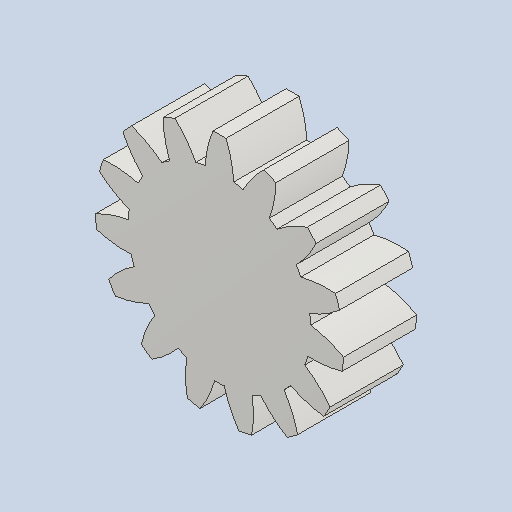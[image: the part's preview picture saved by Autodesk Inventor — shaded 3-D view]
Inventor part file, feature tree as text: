
AUTODESK INVENTOR PART (.ipt)
format: ipt  version: 2023 (Build 270158000, 158)  size: 195,072 bytes
history: native  units: mm (DEFAULTED — no unit token found)
features: plane x3, other x3, sketch x2, extrude x1
ambient origin geometry x8: Origin, YZ Plane, XZ Plane, XY Plane, X Axis, Y Axis, Z Axis, Center Point
bodies: Solid1 (feature_tree)
feature tree (9):
  extrude  "Extrusion1"  Depth=10.0mm TaperAngle=0.0deg
  plane  "Work Plane2"
  plane  "Work Plane8"
  plane  "Work Plane9"
  other  "Spur Gear"
  sketch  "Sketch1"  dims[d0=34.0mm d1=10.0mm d2=0.0mm]
  sketch  "Sketch2"  dims[d3=30.0mm d4=10.0mm d5=0.0mm d16=45.0mm d17=0.0mm d34=2.094395mm d39=0.0mm d41=0.0mm d43=45.0mm d46=45.0mm d47=0.0mm d48=0.0mm]
  other  "Srf1"
  other  "Pitch Diameter"
